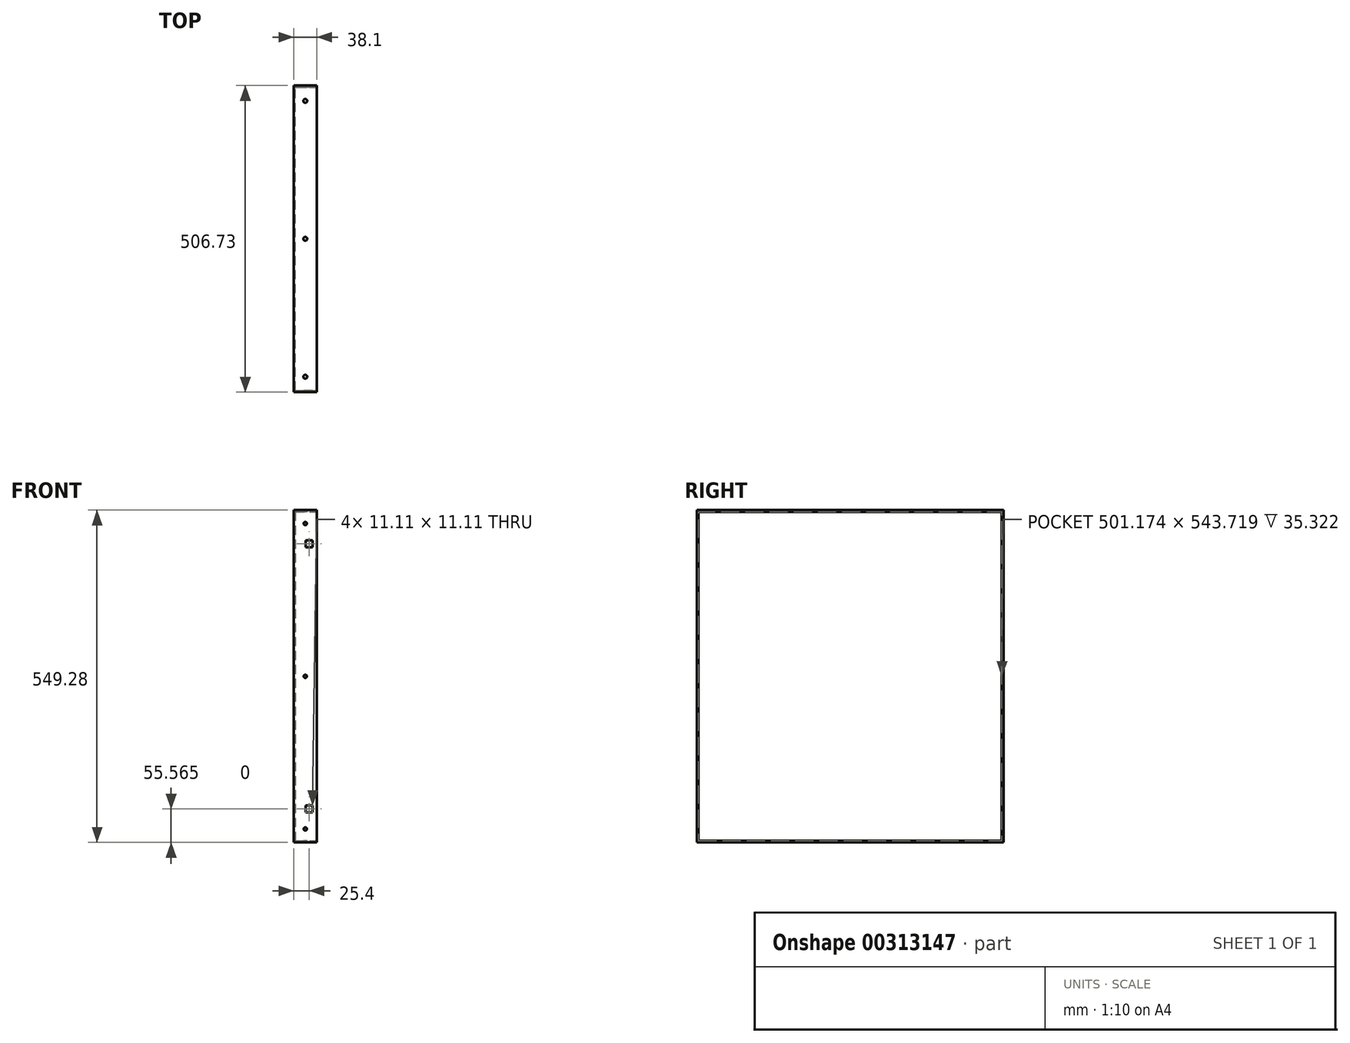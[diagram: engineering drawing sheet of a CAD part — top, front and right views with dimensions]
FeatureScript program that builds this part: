
annotation { "Feature Type Name" : "Feature", "Feature Type Description" : "" }
export const myFeature = defineFeature(function(context is Context, id is Id, definition is map)
    precondition{}
    {
        {
            var Q0;
            Q0=qCreatedBy(makeId("Top.planeOp"),FACE);
            var sketch = newSketch(context, id + "F0", { "sketchPlane" : qUnion([Q0])});
            skLineSegment(sketch, "E0.bottom", {"start": v(0, 0) * mm, "end": v(38.1, 0) * mm});
            skLineSegment(sketch, "E0.top", {"start": v(0, 506.73) * mm, "end": v(38.1, 506.73) * mm});
            skLineSegment(sketch, "E0.left", {"start": v(0, 0) * mm, "end": v(0, 506.73) * mm});
            skLineSegment(sketch, "E0.right", {"start": v(38.1, 0) * mm, "end": v(38.1, 506.73) * mm});
            skSolve(sketch);
        }
        {
            var Q0;
            Q0=qSketchRegion(id+"F0",true);
            extrude(context, id + "F1", {"entities" : qUnion([Q0]), "endBound" : BoundingType.SYMMETRIC, "depth" : 549.27 * mm});
        }
        {
            var Q0;
            Q0=makeQuery(id+"F1.opExtrude","SWEPT_FACE",FACE,{"disambiguationData":[OSD([sQuery(id+"F0.wireOp",EDGE,"E0.right")])]});
            var Q1;
            Q1=makeQuery(id+"F1.opExtrude","SWEPT_FACE",FACE,{"disambiguationData":[OSD([sQuery(id+"F0.wireOp",EDGE,"06e66f88-2ae3-45e9-895b-eb5daa671fde.1.0.3")])]});
            shell(context, id + "F2", {"entities" : qUnion([Q0, Q1]), "thickness" : 2.78 * mm});
        }
        {
            var Q0;
            Q0=makeQuery(id+"F1.opExtrude","SWEPT_FACE",FACE,{"disambiguationData":[OSD([sQuery(id+"F0.wireOp",EDGE,"E0.top")])]});
            var sketch = newSketch(context, id + "F3", { "sketchPlane" : qUnion([Q0])});
            skCircle(sketch, "E1", {"center": v(-19.05, 252.41) * mm, "radius": 2.58 * mm});
            skPoint(sketch, "E1.centerSnap0", {"position": v(-19.05, 274.64) * mm});
            skCircle(sketch, "E2", {"center": v(-19.05, 0) * mm, "radius": 2.58 * mm});
            skCircle(sketch, "E3", {"center": v(-19.05, -252.41) * mm, "radius": 2.58 * mm});
            skLineSegment(sketch, "E4", {"start": v(-19.05, 252.41) * mm, "end": v(-19.05, -252.41) * mm, "construction": true});
            skCircle(sketch, "E5", {"center": v(-25.4, 219.08) * mm, "radius": 2.58 * mm, "construction": true});
            skCircle(sketch, "E6", {"center": v(-25.4, -219.07) * mm, "radius": 2.58 * mm, "construction": true});
            skLineSegment(sketch, "E7", {"start": v(-25.4, -219.07) * mm, "end": v(-25.4, 219.08) * mm, "construction": true});
            skPoint(sketch, "E8", {"position": v(-25.4, 0) * mm});
            skLineSegment(sketch, "E9.bottom", {"start": v(-30.96, 213.52) * mm, "end": v(-19.84, 213.52) * mm});
            skLineSegment(sketch, "E9.top", {"start": v(-30.96, 224.63) * mm, "end": v(-19.84, 224.63) * mm});
            skLineSegment(sketch, "E9.left", {"start": v(-30.96, 213.52) * mm, "end": v(-30.96, 224.63) * mm});
            skLineSegment(sketch, "E9.right", {"start": v(-19.84, 213.52) * mm, "end": v(-19.84, 224.63) * mm});
            skLineSegment(sketch, "E10.bottom", {"start": v(-30.96, -224.63) * mm, "end": v(-19.84, -224.63) * mm});
            skLineSegment(sketch, "E10.top", {"start": v(-30.96, -213.52) * mm, "end": v(-19.84, -213.52) * mm});
            skLineSegment(sketch, "E10.left", {"start": v(-30.96, -224.63) * mm, "end": v(-30.96, -213.52) * mm});
            skLineSegment(sketch, "E10.right", {"start": v(-19.84, -224.63) * mm, "end": v(-19.84, -213.52) * mm});
            skSolve(sketch);
        }
        {
            var Q0;
            Q0 = qSketchRegion(id + "F3", true);
            extrude(context, id + "F4", {"entities" : qUnion([Q0]), "operationType" : NewBodyOperationType.REMOVE, "endBound" : BoundingType.THROUGH_ALL, "oppositeDirection" : true, "depth" : 25.4 * mm});
        }
        {
            var Q0;
            Q0=makeQuery(id+"F1.opExtrude","CAP_FACE",FACE,{"disambiguationData":[OSD([sQuery(id+"F0.wireOp",EDGE,"E0.bottom"),sQuery(id+"F0.wireOp",EDGE,"E0.top"),sQuery(id+"F0.wireOp",EDGE,"E0.left"),sQuery(id+"F0.wireOp",EDGE,"E0.right")])],"isStart":false});
            var sketch = newSketch(context, id + "F5", { "sketchPlane" : qUnion([Q0])});
            skCircle(sketch, "E11", {"center": v(19.05, 481.33) * mm, "radius": 3.17 * mm});
            skPoint(sketch, "E11.centerSnap0", {"position": v(19.05, 506.73) * mm});
            skCircle(sketch, "E12", {"center": v(19.05, 253.37) * mm, "radius": 3.17 * mm});
            skCircle(sketch, "E13", {"center": v(19.05, 25.4) * mm, "radius": 3.17 * mm});
            skLineSegment(sketch, "E14", {"start": v(19.05, 481.33) * mm, "end": v(19.05, 25.4) * mm, "construction": true});
            skSolve(sketch);
        }
        {
            var Q0;
            Q0 = qSketchRegion(id + "F5", true);
            extrude(context, id + "F6", {"entities" : qUnion([Q0]), "operationType" : NewBodyOperationType.REMOVE, "endBound" : BoundingType.THROUGH_ALL, "oppositeDirection" : true, "depth" : 25.4 * mm});
        }
    });
